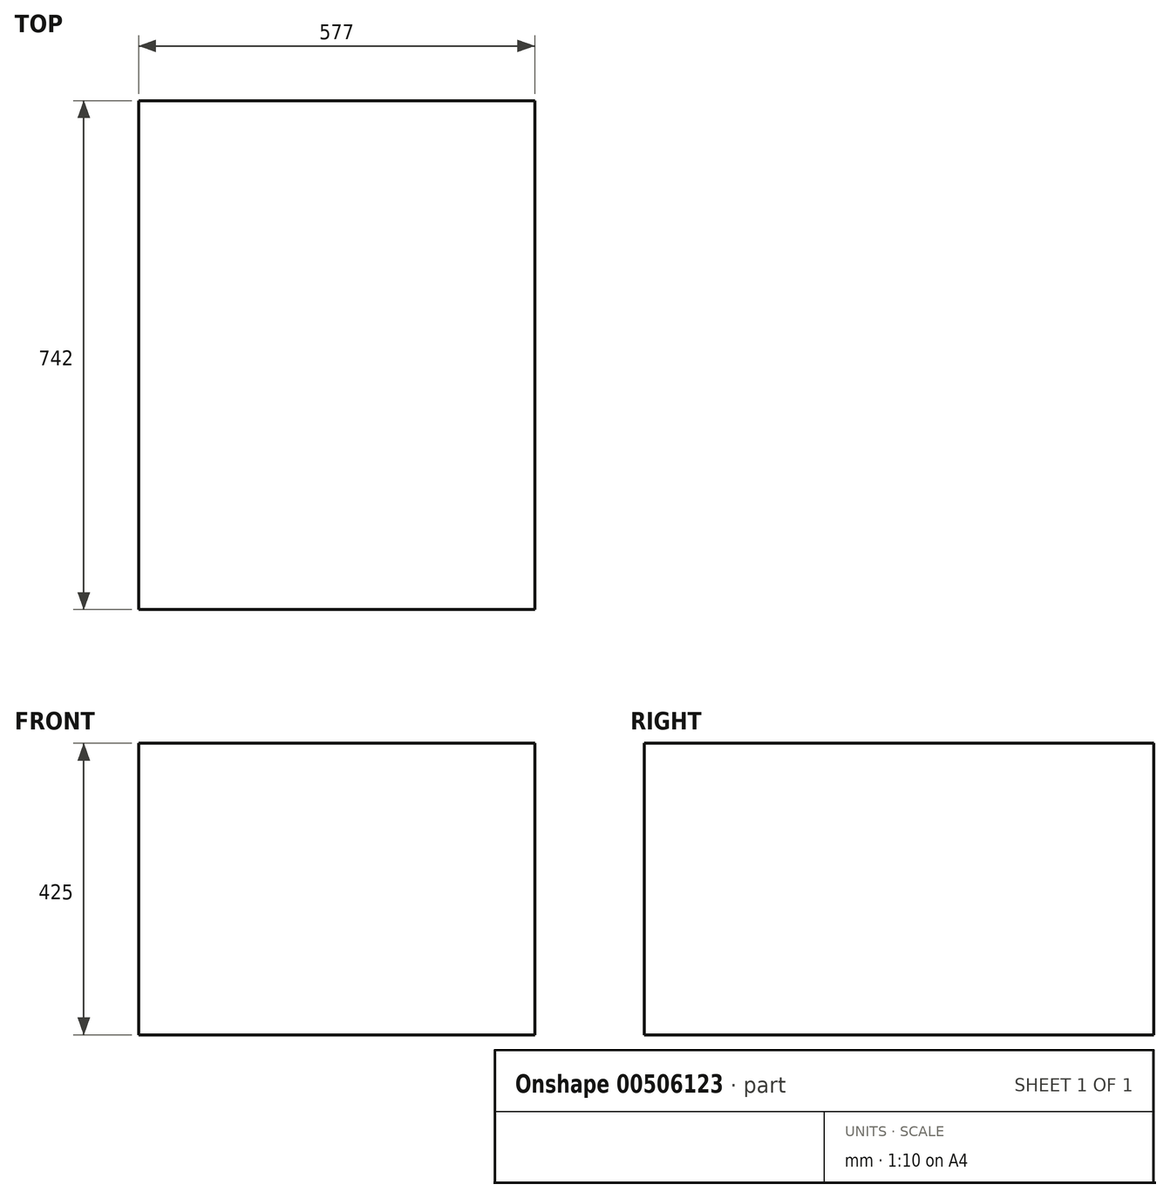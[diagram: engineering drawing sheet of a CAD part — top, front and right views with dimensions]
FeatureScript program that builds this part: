
annotation { "Feature Type Name" : "Feature", "Feature Type Description" : "" }
export const myFeature = defineFeature(function(context is Context, id is Id, definition is map)
    precondition{}
    {
        {
            var Q0;
            Q0=qCreatedBy(makeId("Top.planeOp"),FACE);
            var sketch = newSketch(context, id + "F0", { "sketchPlane" : qUnion([Q0])});
            skLineSegment(sketch, "E0.bottom", {"start": v(288.5, -371) * mm, "end": v(-288.5, -371) * mm});
            skLineSegment(sketch, "E0.top", {"start": v(288.5, 371) * mm, "end": v(-288.5, 371) * mm});
            skLineSegment(sketch, "E0.left", {"start": v(288.5, -371) * mm, "end": v(288.5, 371) * mm});
            skLineSegment(sketch, "E0.right", {"start": v(-288.5, -371) * mm, "end": v(-288.5, 371) * mm});
            skPoint(sketch, "E0.middle", {"position": v(0, 0) * mm});
            skSolve(sketch);
        }
        {
            var Q0;
            Q0=makeQuery(id+"F0.imprint","IMPRINT",FACE,{"disambiguationData":[TD([[makeQuery(id+"F0.imprint","IMPRINT",EDGE,{"derivedFrom":sQuery(id+"F0.wireOp",EDGE,"E0.bottom")}),-1.0]])]});
            extrude(context, id + "F1", {"entities" : qUnion([Q0]), "depth" : 425 * mm});
        }
    });
